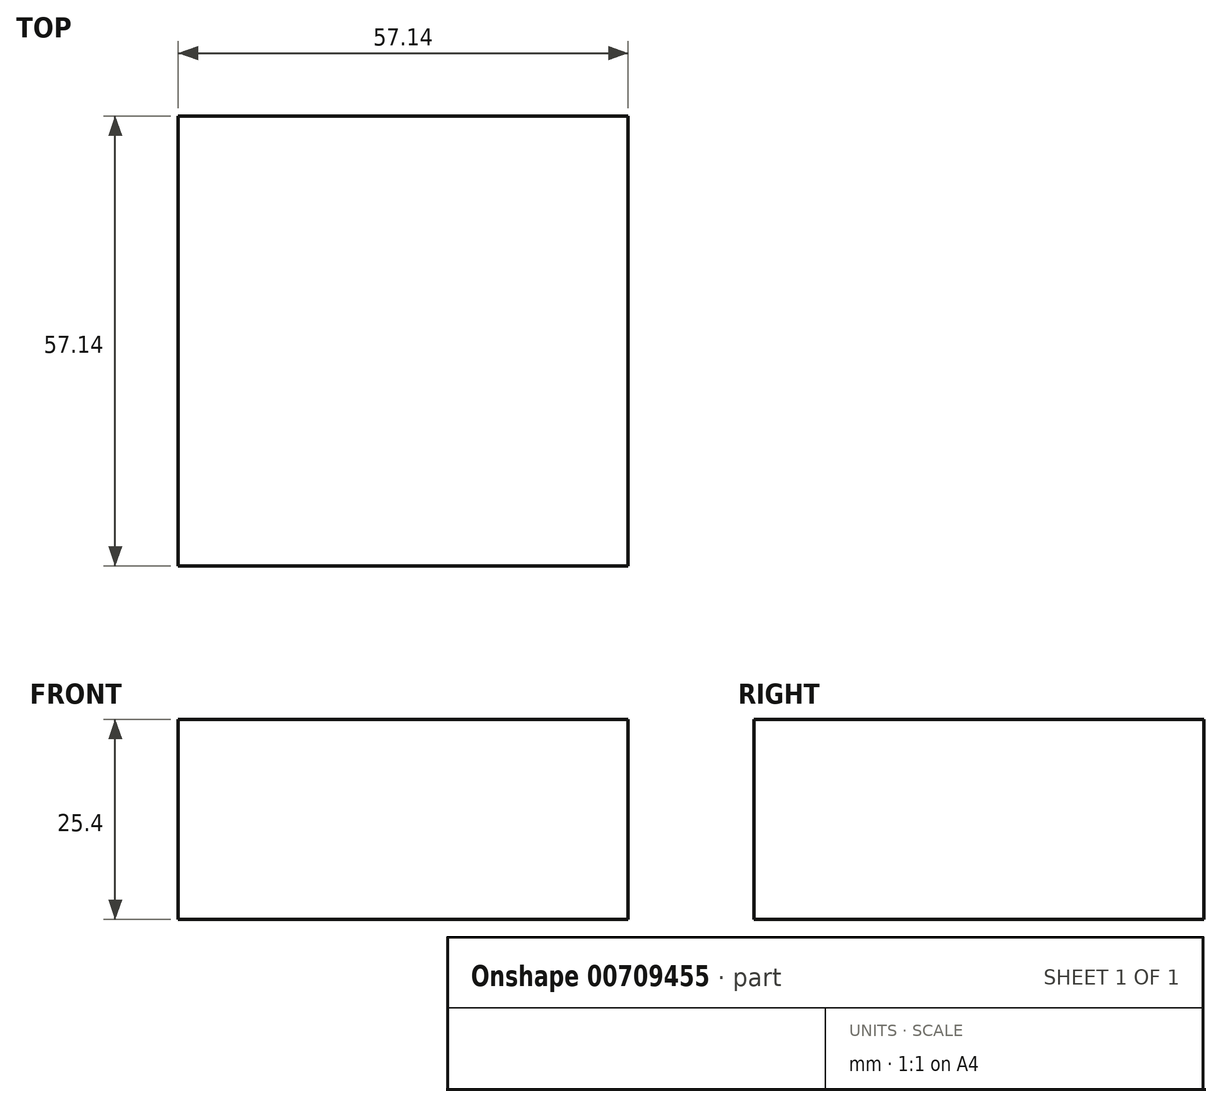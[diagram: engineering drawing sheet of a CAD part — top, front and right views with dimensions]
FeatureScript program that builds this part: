
annotation { "Feature Type Name" : "Feature", "Feature Type Description" : "" }
export const myFeature = defineFeature(function(context is Context, id is Id, definition is map)
    precondition{}
    {
        {
            var Q0;
            Q0=qCreatedBy(makeId("Top.planeOp"),FACE);
            var sketch = newSketch(context, id + "F0", { "sketchPlane" : qUnion([Q0])});
            skLineSegment(sketch, "E0.bottom", {"start": v(28.58, -28.57) * mm, "end": v(-28.57, -28.58) * mm});
            skLineSegment(sketch, "E0.top", {"start": v(28.57, 28.58) * mm, "end": v(-28.58, 28.58) * mm});
            skLineSegment(sketch, "E0.left", {"start": v(28.58, -28.57) * mm, "end": v(28.57, 28.58) * mm});
            skLineSegment(sketch, "E0.right", {"start": v(-28.57, -28.58) * mm, "end": v(-28.58, 28.58) * mm});
            skPoint(sketch, "E0.middle", {"position": v(0, 0) * mm});
            skSolve(sketch);
        }
        {
            var Q0;
            Q0=makeQuery(id+"F0.imprint","IMPRINT",FACE,{"disambiguationData":[TD([[makeQuery(id+"F0.imprint","IMPRINT",EDGE,{"derivedFrom":sQuery(id+"F0.wireOp",EDGE,"E0.bottom")}),-1.0]])]});
            extrude(context, id + "F1", {"entities" : qUnion([Q0]), "depth" : 25.4 * mm, "offsetDistance" : 25.4 * mm});
        }
    });
